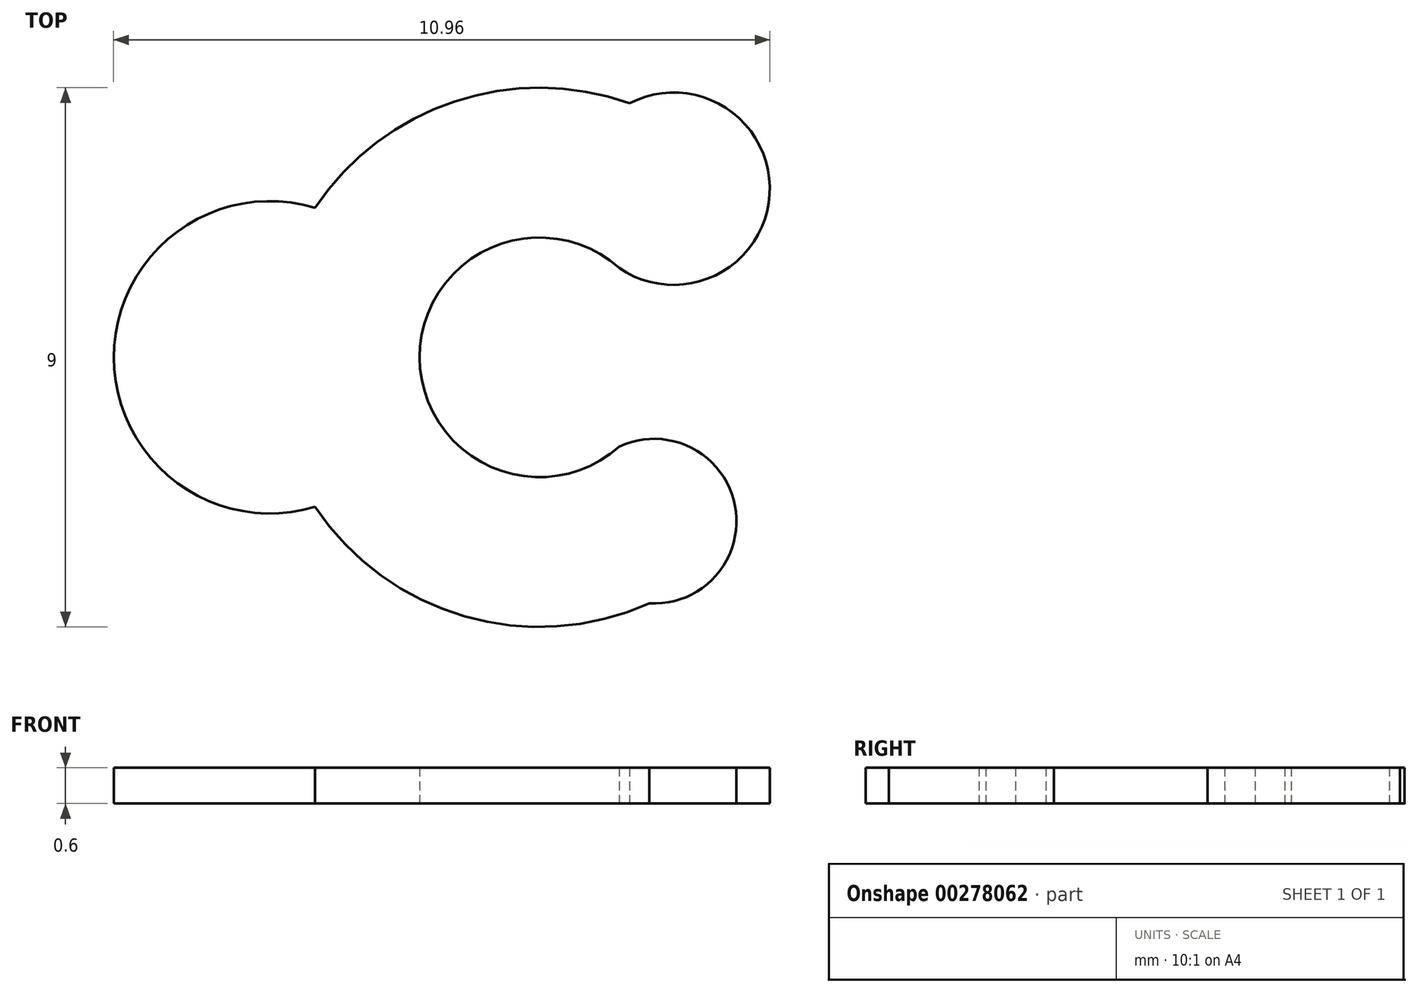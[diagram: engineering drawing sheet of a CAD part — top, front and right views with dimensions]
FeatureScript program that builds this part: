
annotation { "Feature Type Name" : "Feature", "Feature Type Description" : "" }
export const myFeature = defineFeature(function(context is Context, id is Id, definition is map)
    precondition{}
    {
        {
            var Q0;
            Q0=qCreatedBy(makeId("Top.planeOp"),FACE);
            var sketch = newSketch(context, id + "F0", { "sketchPlane" : qUnion([Q0])});
            skArc(sketch, "E0", {"start": v(-14.06, -2.5) * mm, "mid": v(-11.57, -4.32) * mm, "end": v(-8.48, -4.1) * mm});
            skArc(sketch, "E1", {"start": v(-14.06, 2.5) * mm, "mid": v(-17.43, 0) * mm, "end": v(-14.06, -2.5) * mm});
            skArc(sketch, "E2", {"start": v(-8.99, 1.5) * mm, "mid": v(-12.32, 0) * mm, "end": v(-8.98, -1.49) * mm});
            skPoint(sketch, "E3.startSnap0", {"position": v(-7.09, 0.9) * mm});
            skArc(sketch, "E4.trimOffspring", {"start": v(-8.82, 4.24) * mm, "mid": v(-11.74, 4.27) * mm, "end": v(-14.06, 2.5) * mm});
            skArc(sketch, "E5", {"start": v(-8.59, -4.15) * mm, "mid": v(-8.53, -4.13) * mm, "end": v(-8.48, -4.1) * mm});
            skPoint(sketch, "E6.orphan", {"position": v(-7.09, -3.13) * mm});
            skArc(sketch, "E7", {"start": v(-8.99, 1.5) * mm, "mid": v(-6.47, 2.72) * mm, "end": v(-8.82, 4.24) * mm});
            skArc(sketch, "E8", {"start": v(-8.48, -4.1) * mm, "mid": v(-7.05, -2.48) * mm, "end": v(-8.98, -1.49) * mm});
            skSolve(sketch);
        }
        {
            var Q0;
            Q0=makeQuery(id+"F0.imprint","IMPRINT",FACE,{"disambiguationData":[TD([[makeQuery(id+"F0.imprint","IMPRINT",EDGE,{"derivedFrom":sQuery(id+"F0.wireOp",EDGE,"E0")}),1.0]])]});
            extrude(context, id + "F1", {"entities" : qUnion([Q0]), "depth" : .6 * mm});
        }
    });
